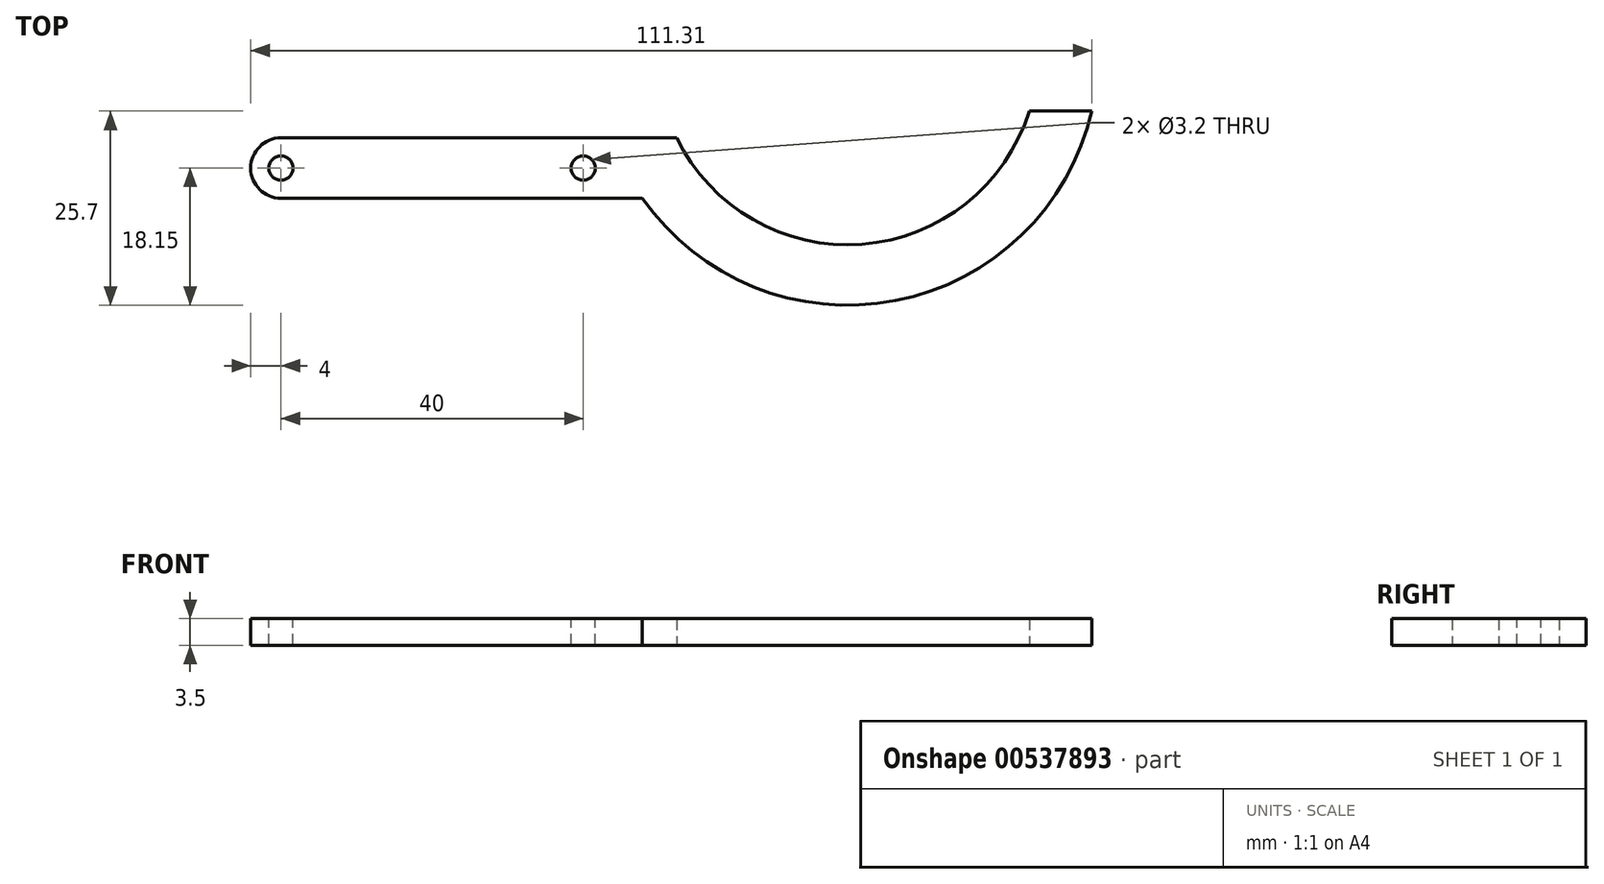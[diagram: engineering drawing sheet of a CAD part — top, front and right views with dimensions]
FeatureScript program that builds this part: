
annotation { "Feature Type Name" : "Feature", "Feature Type Description" : "" }
export const myFeature = defineFeature(function(context is Context, id is Id, definition is map)
    precondition{}
    {
        {
            var Q0;
            Q0=qCreatedBy(makeId("Top.planeOp"),FACE);
            var sketch = newSketch(context, id + "F0", { "sketchPlane" : qUnion([Q0])});
            skLineSegment(sketch, "E0.bottom", {"start": v(50, -4) * mm, "end": v(-50, -4) * mm});
            skLineSegment(sketch, "E0.top", {"start": v(50, 4) * mm, "end": v(-50, 4) * mm});
            skLineSegment(sketch, "E0.left", {"start": v(50, -4) * mm, "end": v(50, 4) * mm});
            skLineSegment(sketch, "E0.right", {"start": v(-50, -4) * mm, "end": v(-50, 4) * mm});
            skPoint(sketch, "E0.middle", {"position": v(0, 0) * mm});
            skCircle(sketch, "E1", {"center": v(-50, 0) * mm, "radius": 4 * mm});
            skCircle(sketch, "E2", {"center": v(50, 0) * mm, "radius": 4 * mm});
            skLineSegment(sketch, "E3", {"start": v(0, 0) * mm, "end": v(50, 0) * mm});
            skLineSegment(sketch, "E4", {"start": v(25, 0) * mm, "end": v(25, 15) * mm});
            skCircle(sketch, "E5", {"center": v(25, 15) * mm, "radius": 33.15 * mm});
            skCircle(sketch, "E6", {"center": v(25, 15) * mm, "radius": 25.15 * mm});
            skLineSegment(sketch, "E7", {"start": v(49.03, 7.55) * mm, "end": v(57.3, 7.55) * mm});
            skSolve(sketch);
        }
        {
            var Q0;
            {var subQ0=sQuery(id+"F0.wireOp",EDGE,"E0.right");Q0=makeQuery(id+"F0.imprint","IMPRINT",FACE,{"disambiguationData":[TD([[makeQuery(id+"F0.imprint","IMPRINT",EDGE,{"derivedFrom":subQ0}),1.0]])]});}
            var Q1;
            {var subQ0=sQuery(id+"F0.wireOp",EDGE,"E0.right");Q1=makeQuery(id+"F0.imprint","IMPRINT",FACE,{"disambiguationData":[TD([[makeQuery(id+"F0.imprint","IMPRINT",EDGE,{"derivedFrom":subQ0}),-1.0]])]});}
            var Q2;
            {var subQ2=sQuery(id+"F0.wireOp",EDGE,"E0.bottom");var subQ4=sQuery(id+"F0.wireOp",EDGE,"E5");var subQ5=makeQuery(id+"F0.imprint","INTERSECT",VERTEX,{"derivedFrom":[subQ2,subQ4]});Q2=makeQuery(id+"F0.imprint","IMPRINT",FACE,{"disambiguationData":[TD([[makeQuery(id+"F0.imprint","IMPRINT",EDGE,{"disambiguationData":[TD([[subQ5,1.0]])],"derivedFrom":subQ4}),-1.0]])]});}
            var Q3;
            {var subQ4=sQuery(id+"F0.wireOp",EDGE,"E5");var subQ5=sQuery(id+"F0.wireOp",EDGE,"E0.bottom");var subQ6=makeQuery(id+"F0.imprint","INTERSECT",VERTEX,{"derivedFrom":[subQ5,subQ4]});Q3=makeQuery(id+"F0.imprint","IMPRINT",FACE,{"disambiguationData":[TD([[makeQuery(id+"F0.imprint","IMPRINT",EDGE,{"disambiguationData":[TD([[subQ6,1.0]])],"derivedFrom":subQ5}),-1.0]])]});}
            var Q4;
            {var subQ1=sQuery(id+"F0.wireOp",EDGE,"E0.bottom");var subQ3=sQuery(id+"F0.wireOp",EDGE,"E5");var subQ5=makeQuery(id+"F0.imprint","INTERSECT",VERTEX,{"derivedFrom":[subQ1,subQ3]});Q4=makeQuery(id+"F0.imprint","IMPRINT",FACE,{"disambiguationData":[TD([[makeQuery(id+"F0.imprint","IMPRINT",EDGE,{"disambiguationData":[TD([[subQ5,1.0]])],"derivedFrom":subQ1}),1.0]])]});}
            var Q5;
            {var subQ0=sQuery(id+"F0.wireOp",EDGE,"E2");var subQ5=sQuery(id+"F0.wireOp",EDGE,"E3");var subQ6=makeQuery(id+"F0.imprint","INTERSECT",VERTEX,{"derivedFrom":[subQ0,subQ5]});Q5=makeQuery(id+"F0.imprint","IMPRINT",FACE,{"disambiguationData":[TD([[makeQuery(id+"F0.imprint","IMPRINT",EDGE,{"disambiguationData":[TD([[subQ6,1.0]])],"derivedFrom":subQ5}),-1.0]])]});}
            var Q6;
            {var subQ1=sQuery(id+"F0.wireOp",EDGE,"E0.left");var subQ3=sQuery(id+"F0.wireOp",EDGE,"E3");var subQ4=makeQuery(id+"F0.imprint","INTERSECT",VERTEX,{"derivedFrom":[subQ1,subQ3]});Q6=makeQuery(id+"F0.imprint","IMPRINT",FACE,{"disambiguationData":[TD([[makeQuery(id+"F0.imprint","IMPRINT",EDGE,{"disambiguationData":[TD([[subQ4,1.0]])],"derivedFrom":subQ3}),-1.0]])]});}
            var Q7;
            {var subQ1=sQuery(id+"F0.wireOp",EDGE,"E0.left");var subQ3=makeQuery(id+"F0.imprint","INTERSECT",VERTEX,{"derivedFrom":[subQ1,sQuery(id+"F0.wireOp",EDGE,"E3")]});Q7=makeQuery(id+"F0.imprint","IMPRINT",FACE,{"disambiguationData":[TD([[makeQuery(id+"F0.imprint","IMPRINT",EDGE,{"disambiguationData":[TD([[subQ3,1.0]])],"derivedFrom":subQ1}),-1.0]])]});}
            var Q8;
            {var subQ0=sQuery(id+"F0.wireOp",EDGE,"E2");var subQ5=makeQuery(id+"F0.imprint","INTERSECT",VERTEX,{"derivedFrom":[subQ0,sQuery(id+"F0.wireOp",EDGE,"E6")]});Q8=makeQuery(id+"F0.imprint","IMPRINT",FACE,{"disambiguationData":[TD([[makeQuery(id+"F0.imprint","IMPRINT",EDGE,{"disambiguationData":[TD([[subQ5,-1.0]])],"derivedFrom":subQ0}),1.0]])]});}
            var Q9;
            {var subQ1=sQuery(id+"F0.wireOp",EDGE,"E0.top");var subQ3=sQuery(id+"F0.wireOp",EDGE,"E6");var subQ4=makeQuery(id+"F0.imprint","INTERSECT",VERTEX,{"disambiguationData":[OD(0.0)],"derivedFrom":[subQ1,subQ3]});Q9=makeQuery(id+"F0.imprint","IMPRINT",FACE,{"disambiguationData":[TD([[makeQuery(id+"F0.imprint","IMPRINT",EDGE,{"disambiguationData":[TD([[subQ4,1.0]])],"derivedFrom":subQ3}),-1.0]])]});}
            var Q10;
            {var subQ0=sQuery(id+"F0.wireOp",EDGE,"E6");var subQ1=sQuery(id+"F0.wireOp",EDGE,"E2");var subQ2=makeQuery(id+"F0.imprint","INTERSECT",VERTEX,{"derivedFrom":[subQ1,subQ0]});Q10=makeQuery(id+"F0.imprint","IMPRINT",FACE,{"disambiguationData":[TD([[makeQuery(id+"F0.imprint","IMPRINT",EDGE,{"disambiguationData":[TD([[subQ2,-1.0]])],"derivedFrom":subQ1}),-1.0]])]});}
            var Q11;
            {var subQ0=sQuery(id+"F0.wireOp",EDGE,"E7");Q11=makeQuery(id+"F0.imprint","IMPRINT",FACE,{"disambiguationData":[TD([[makeQuery(id+"F0.imprint","IMPRINT",EDGE,{"derivedFrom":subQ0}),-1.0]])]});}
            extrude(context, id + "F1", {"entities" : qUnion([Q0, Q1, Q2, Q3, Q4, Q5, Q6, Q7, Q8, Q9, Q10, Q11]), "depth" : 3.5 * mm, "offsetDistance" : 25 * mm});
        }
        {
            var Q0;
            Q0=makeQuery(id+"F1.opExtrude","CAP_FACE",FACE,{"disambiguationData":[OSD([sQuery(id+"F0.wireOp",EDGE,"E0.bottom"),sQuery(id+"F0.wireOp",EDGE,"E0.top"),sQuery(id+"F0.wireOp",EDGE,"E1"),sQuery(id+"F0.wireOp",EDGE,"E2")])],"isStart":false});
            var sketch = newSketch(context, id + "F2", { "sketchPlane" : qUnion([Q0])});
            skLineSegment(sketch, "E8.bottom", {"start": v(-50, 4) * mm, "end": v(50, 4) * mm});
            skLineSegment(sketch, "E8.top", {"start": v(-50, -4) * mm, "end": v(-2.17, -4) * mm});
            skLineSegment(sketch, "E8.left", {"start": v(-50, 4) * mm, "end": v(-50, -4) * mm});
            skCircle(sketch, "E9", {"center": v(-50, 0) * mm, "radius": 1.6 * mm});
            skLineSegment(sketch, "E10", {"start": v(-50, 0) * mm, "end": v(-10, 0) * mm});
            skCircle(sketch, "E11", {"center": v(-10, 0) * mm, "radius": 1.6 * mm});
            skSolve(sketch);
        }
        {
            var Q0;
            {var subQ0=sQuery(id+"F2.wireOp",EDGE,"E10");var subQ1=sQuery(id+"F2.wireOp",EDGE,"E8.left");var subQ2=makeQuery(id+"F2.imprint","INTERSECT",VERTEX,{"derivedFrom":[subQ1,subQ0]});Q0=makeQuery(id+"F2.imprint","IMPRINT",FACE,{"disambiguationData":[TD([[makeQuery(id+"F2.imprint","IMPRINT",EDGE,{"disambiguationData":[TD([[subQ2,1.0]])],"derivedFrom":subQ1}),1.0]])]});}
            var Q1;
            {var subQ0=sQuery(id+"F2.wireOp",EDGE,"E8.left");var subQ1=makeQuery(id+"F2.imprint","INTERSECT",VERTEX,{"derivedFrom":[subQ0,sQuery(id+"F2.wireOp",EDGE,"E10")]});Q1=makeQuery(id+"F2.imprint","IMPRINT",FACE,{"disambiguationData":[TD([[makeQuery(id+"F2.imprint","IMPRINT",EDGE,{"disambiguationData":[TD([[subQ1,1.0]])],"derivedFrom":subQ0}),-1.0]])]});}
            var Q2;
            Q2=makeQuery(id+"F2.imprint","IMPRINT",FACE,{"disambiguationData":[TD([[makeQuery(id+"F2.imprint","IMPRINT",EDGE,{"derivedFrom":sQuery(id+"F2.wireOp",EDGE,"E11")}),1.0]])]});
            var Q3;
            {var subQ0=sQuery(id+"F2.wireOp",EDGE,"k93yb0rX-Fjv0-j3XL-3Sc2-wuIDpt9v61p8");var subQ1=sQuery(id+"F2.wireOp",EDGE,"E8.right");var subQ2=makeQuery(id+"F2.imprint","INTERSECT",VERTEX,{"disambiguationData":[OD(0.0)],"derivedFrom":[subQ1,subQ0]});Q3=makeQuery(id+"F2.imprint","IMPRINT",FACE,{"disambiguationData":[TD([[makeQuery(id+"F2.imprint","IMPRINT",EDGE,{"disambiguationData":[TD([[subQ2,-1.0]])],"derivedFrom":subQ1}),-1.0]])]});}
            var Q4;
            {var subQ0=sQuery(id+"F2.wireOp",EDGE,"k93yb0rX-Fjv0-j3XL-3Sc2-wuIDpt9v61p8");var subQ1=sQuery(id+"F2.wireOp",EDGE,"E8.right");var subQ2=makeQuery(id+"F2.imprint","INTERSECT",VERTEX,{"disambiguationData":[OD(0.0)],"derivedFrom":[subQ1,subQ0]});Q4=makeQuery(id+"F2.imprint","IMPRINT",FACE,{"disambiguationData":[TD([[makeQuery(id+"F2.imprint","IMPRINT",EDGE,{"disambiguationData":[TD([[subQ2,-1.0]])],"derivedFrom":subQ1}),1.0]])]});}
            var Q5;
            {var subQ0=sQuery(id+"F2.wireOp",EDGE,"E10");var subQ1=sQuery(id+"F2.wireOp",EDGE,"E8.left");var subQ2=makeQuery(id+"F2.imprint","INTERSECT",VERTEX,{"derivedFrom":[subQ1,subQ0]});Q5=makeQuery(id+"F2.imprint","IMPRINT",FACE,{"disambiguationData":[TD([[makeQuery(id+"F2.imprint","IMPRINT",EDGE,{"disambiguationData":[TD([[subQ2,-1.0]])],"derivedFrom":subQ1}),1.0]])]});}
            extrude(context, id + "F3", {"entities" : qUnion([Q0, Q1, Q2, Q3, Q4, Q5]), "operationType" : NewBodyOperationType.REMOVE, "endBound" : BoundingType.THROUGH_ALL, "oppositeDirection" : true, "depth" : 25 * mm, "offsetDistance" : 25 * mm});
        }
    });
